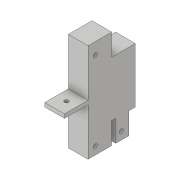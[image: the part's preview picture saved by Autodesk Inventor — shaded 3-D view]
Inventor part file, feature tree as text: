
AUTODESK INVENTOR PART (.ipt)
format: ipt  version: 2019.4 (Build 234330000, 330)  size: 131,072 bytes
history: native  units: mm
features: extrude x2, sketch x2, projected_geometry x1
ambient origin geometry x8: Origin, YZ Plane, XZ Plane, XY Plane, X Axis, Y Axis, Z Axis, Center Point
bodies: Solid1 (feature_tree)
feature tree (5):
  extrude  "Extrusion1"  Depth=6.0mm
  extrude  "Extrusion2"  Depth=1.0mm
  sketch  "Sketch1"  dims[d0=25.0mm d1=6.0mm]
  sketch  "Sketch2"  dims[d2=1.0mm d3=1.0mm d4=20.0mm d5=14.0mm d6=6.0mm d8=1.0mm d9=6.0mm d10=10.0mm d11=5.0mm d12=0.0mm d13=2.0mm d14=1.0mm d15=5.0mm d16=0.0mm d18=3.0mm d19=5.5mm d20=1.0mm d21=6.6mm]
  projected_geometry  "Projected Loop1"
